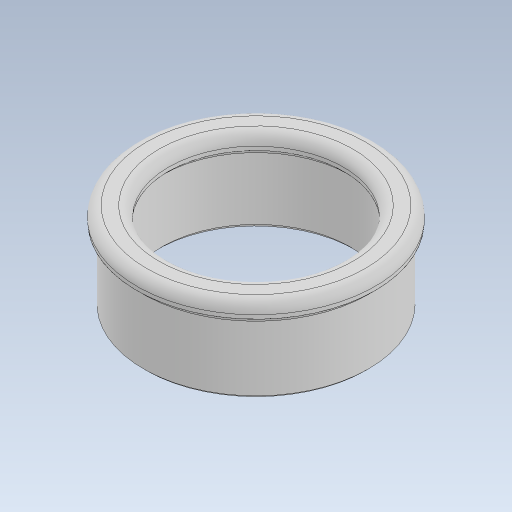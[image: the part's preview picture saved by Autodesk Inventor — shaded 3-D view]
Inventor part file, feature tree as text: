
AUTODESK INVENTOR PART (.ipt)
format: ipt  version: 2023 (Build 270158030, 158C)  size: 172,032 bytes
history: native  units: mm
features: chamfer x4, extrude x2, sketch x2, fillet x1, projected_geometry x1
ambient origin geometry x8: Origin, YZ Plane, XZ Plane, XY Plane, X Axis, Y Axis, Z Axis, Center Point
bodies: Solid1 (feature_tree)
feature tree (10):
  extrude  "Extrusion1"  Depth=38.5mm
  extrude  "Extrusion2"  Depth=15.0mm TaperAngle=0.0deg
  chamfer  "Chamfer1"  Distance=2.0mm Angle=45.0deg
  chamfer  "Chamfer2"  Distance=2.0mm Angle=45.0deg
  chamfer  "Chamfer3"  Distance=0.5mm Angle=45.0deg
  fillet  "Fillet1"  Radius=2.0mm
  chamfer  "Chamfer4"  Distance=2.0mm Angle=45.0deg
  sketch  "Sketch1"  dims[d2=46.0mm d3=38.5mm]
  sketch  "Sketch2"  dims[d4=18.0mm d5=0.872665mm d6=15.0mm d7=0.0mm d8=1.3mm d9=2.0mm d10=45.0deg d11=1.0mm d12=2.0mm d13=45.0deg d14=0.5mm d15=2.0mm d16=45.0deg d17=2.0mm d18=1.3mm d19=2.0mm d20=45.0deg]
  projected_geometry  "Projected Loop1"
